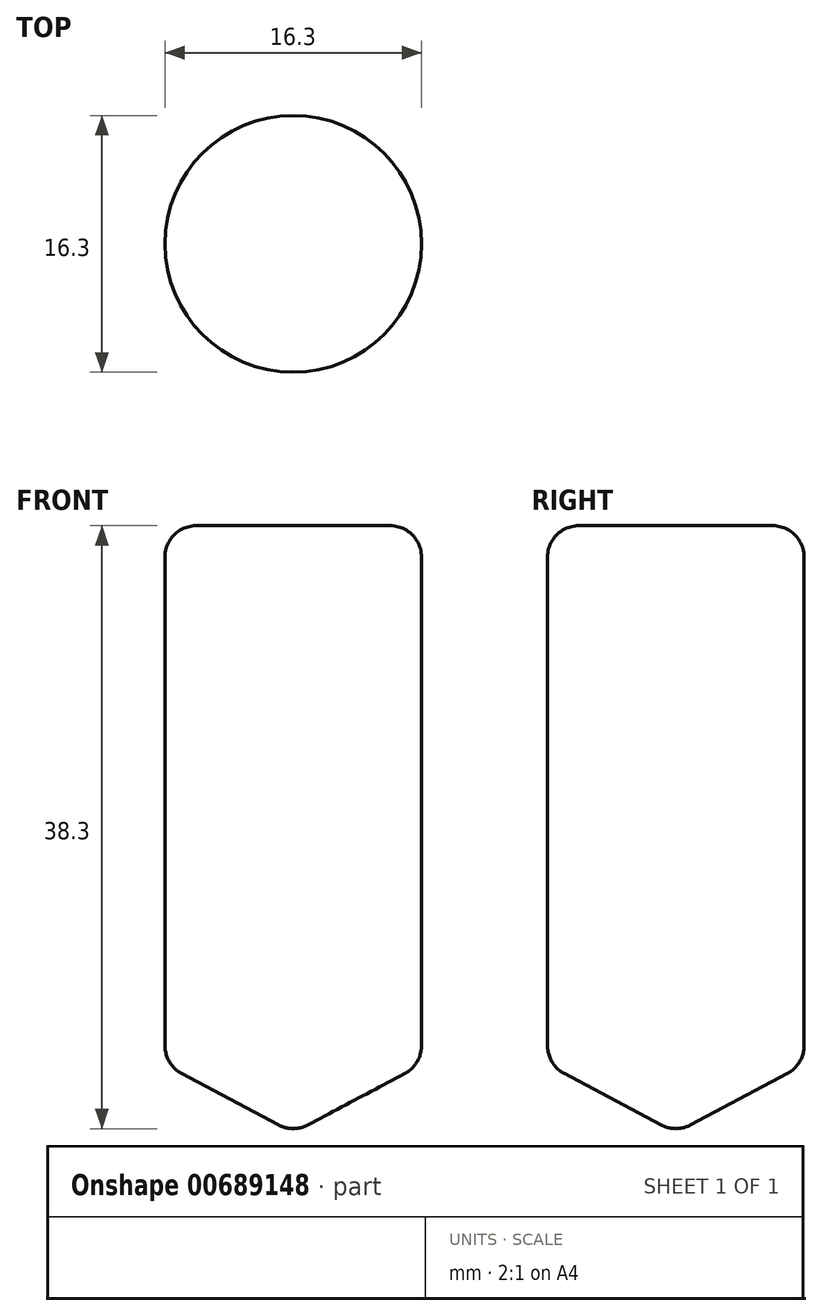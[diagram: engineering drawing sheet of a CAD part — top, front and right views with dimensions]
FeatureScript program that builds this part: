
annotation { "Feature Type Name" : "Feature", "Feature Type Description" : "" }
export const myFeature = defineFeature(function(context is Context, id is Id, definition is map)
    precondition{}
    {
        {
            var Q0;
            Q0=qCreatedBy(makeId("Front.planeOp"),FACE);
            var sketch = newSketch(context, id + "F0", { "sketchPlane" : qUnion([Q0])});
            skLineSegment(sketch, "E0.bottom", {"start": v(-6.15, 0) * mm, "end": v(6.15, 0) * mm, "construction": true});
            skLineSegment(sketch, "E0.top", {"start": v(-6.15, 31.03) * mm, "end": v(6.15, 31.03) * mm, "construction": true});
            skLineSegment(sketch, "E0.left", {"start": v(-6.15, 0) * mm, "end": v(-6.15, 31.03) * mm, "construction": true});
            skLineSegment(sketch, "E0.right", {"start": v(6.15, 0) * mm, "end": v(6.15, 31.03) * mm, "construction": true});
            skLineSegment(sketch, "E1", {"start": v(-6.15, 0) * mm, "end": v(0, -3.27) * mm, "construction": true});
            skLineSegment(sketch, "E2", {"start": v(0, -3.27) * mm, "end": v(6.15, 0) * mm, "construction": true});
            skLineSegment(sketch, "E3.0", {"start": v(-6.15, 33.03) * mm, "end": v(0, 33.03) * mm});
            skLineSegment(sketch, "E3.1", {"start": v(-8.15, 0) * mm, "end": v(-8.15, 31.03) * mm});
            skLineSegment(sketch, "E3.2", {"start": v(8.15, 0) * mm, "end": v(8.15, 31.03) * mm, "construction": true});
            skLineSegment(sketch, "E3.3", {"start": v(0.94, -5.03) * mm, "end": v(7.09, -1.76) * mm, "construction": true});
            skLineSegment(sketch, "E3.4", {"start": v(-7.09, -1.76) * mm, "end": v(-0.94, -5.03) * mm});
            skPoint(sketch, "E4.visualSharp", {"position": v(-8.15, 33.03) * mm});
            skArc(sketch, "E4.filletArc", {"start": v(-6.15, 33.03) * mm, "mid": v(-7.56, 32.45) * mm, "end": v(-8.15, 31.03) * mm});
            skPoint(sketch, "E5.visualSharp", {"position": v(-8.15, -1.2) * mm});
            skArc(sketch, "E5.filletArc", {"start": v(-8.15, 0) * mm, "mid": v(-7.86, -1.03) * mm, "end": v(-7.09, -1.76) * mm});
            skPoint(sketch, "E6.visualSharp", {"position": v(0, -5.53) * mm});
            skArc(sketch, "E6.filletArc", {"start": v(-0.94, -5.03) * mm, "mid": v(-0.48, -5.2) * mm, "end": v(0, -5.27) * mm});
            skPoint(sketch, "E7.visualSharp", {"position": v(8.15, -1.2) * mm});
            skArc(sketch, "E7.filletArc", {"start": v(7.09, -1.76) * mm, "mid": v(7.86, -1.03) * mm, "end": v(8.15, 0) * mm, "construction": true});
            skPoint(sketch, "E8.visualSharp", {"position": v(8.15, 33.03) * mm});
            skArc(sketch, "E8.filletArc", {"start": v(8.15, 31.03) * mm, "mid": v(7.56, 32.45) * mm, "end": v(6.15, 33.03) * mm, "construction": true});
            skLineSegment(sketch, "E9", {"start": v(0, 33.03) * mm, "end": v(6.15, 33.03) * mm, "construction": true});
            skArc(sketch, "E10", {"start": v(0, -5.27) * mm, "mid": v(0.48, -5.2) * mm, "end": v(0.94, -5.03) * mm, "construction": true});
            skLineSegment(sketch, "E11", {"start": v(0, 33.03) * mm, "end": v(0, -5.27) * mm});
            skSolve(sketch);
        }
        {
            var Q0;
            Q0 = qSketchRegion(id + "F0", true);
            var Q1;
            Q1=sQuery(id+"F0.wireOp",EDGE,"E3.0");
            var Q2;
            Q2=sQuery(id+"F0.wireOp",EDGE,"E4.filletArc");
            var Q3;
            Q3=sQuery(id+"F0.wireOp",EDGE,"E3.1");
            var Q4;
            Q4=sQuery(id+"F0.wireOp",EDGE,"E5.filletArc");
            var Q5;
            Q5=sQuery(id+"F0.wireOp",EDGE,"E3.4");
            var Q6;
            Q6=sQuery(id+"F0.wireOp",EDGE,"E6.filletArc");
            var Q7;
            Q7=sQuery(id+"F0.wireOp",EDGE,"E11");
            revolve(context, id + "F1", {"entities" : qUnion([Q0]), "surfaceEntities" : qUnion([Q1, Q2, Q3, Q4, Q5, Q6]), "axis" : qUnion([Q7]), "revolveType" : RevolveType.FULL});
        }
    });
